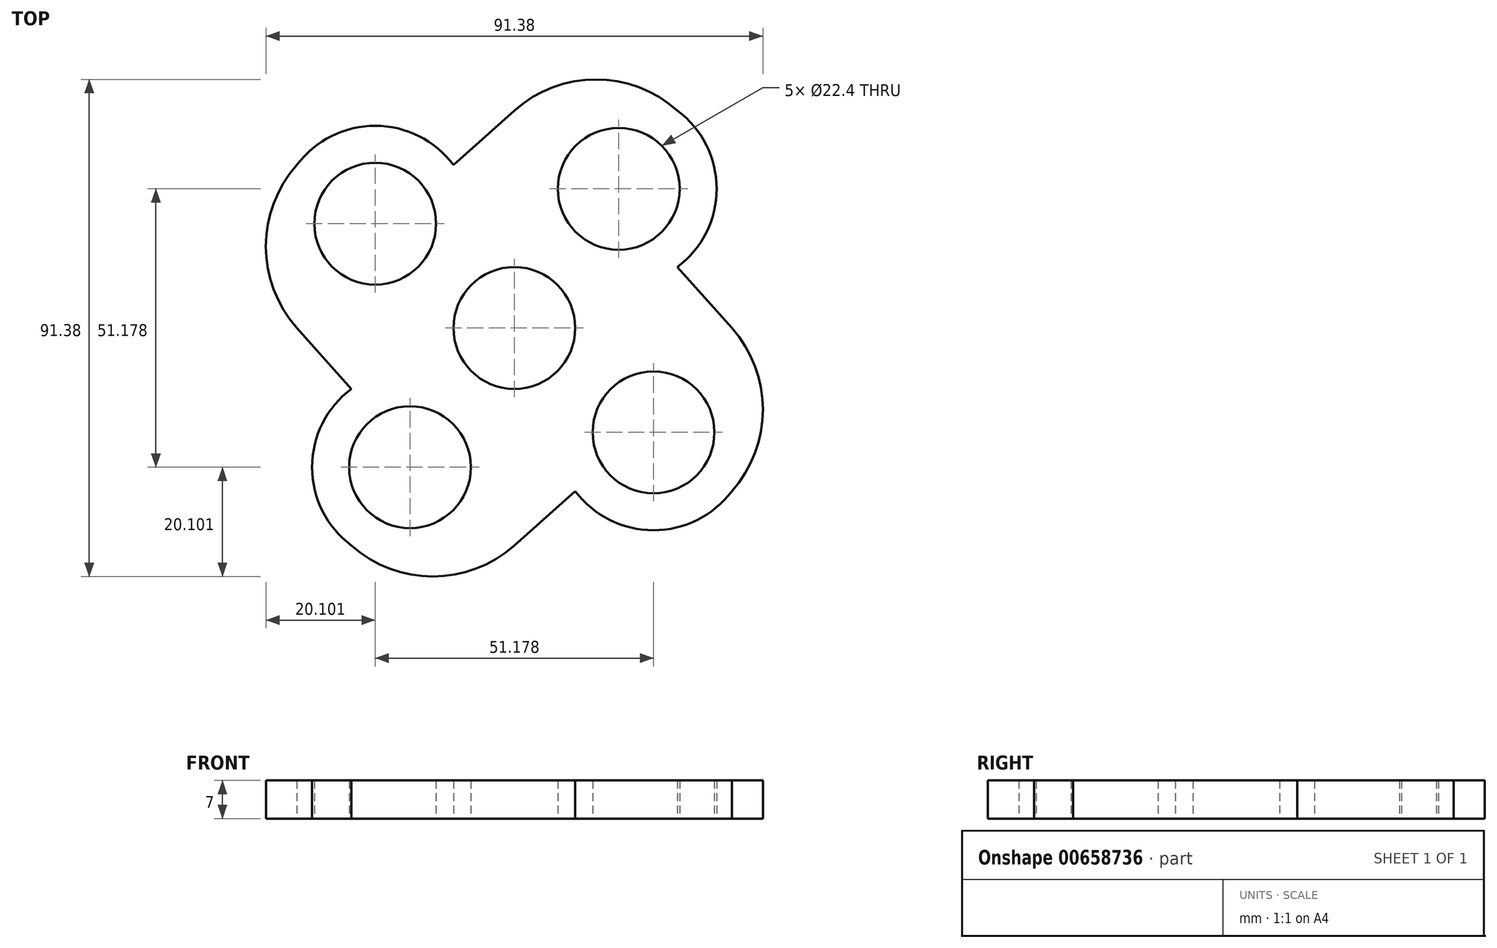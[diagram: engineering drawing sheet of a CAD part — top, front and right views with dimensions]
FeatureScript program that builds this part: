
annotation { "Feature Type Name" : "Feature", "Feature Type Description" : "" }
export const myFeature = defineFeature(function(context is Context, id is Id, definition is map)
    precondition{}
    {
        {
            var Q0;
            Q0=qCreatedBy(makeId("Top.planeOp"),FACE);
            var sketch = newSketch(context, id + "F0", { "sketchPlane" : qUnion([Q0])});
            skCircle(sketch, "E0", {"center": v(0, 0) * mm, "radius": 11.2 * mm});
            skLineSegment(sketch, "E1", {"start": v(0, 11.2) * mm, "end": v(30, 11.2) * mm});
            skLineSegment(sketch, "E2", {"start": v(0, -11.2) * mm, "end": v(-30, -11.2) * mm});
            skLineSegment(sketch, "E3", {"start": v(-11.2, 0) * mm, "end": v(-11.2, 30) * mm});
            skLineSegment(sketch, "E4", {"start": v(11.2, 0) * mm, "end": v(11.2, -30) * mm});
            skLineSegment(sketch, "E5", {"start": v(-11.2, 30) * mm, "end": v(0, 39.98) * mm});
            skLineSegment(sketch, "E6", {"start": v(30, 11.2) * mm, "end": v(39.98, 0) * mm});
            skLineSegment(sketch, "E7", {"start": v(11.2, -30) * mm, "end": v(0, -39.98) * mm});
            skLineSegment(sketch, "E8", {"start": v(-30, -11.2) * mm, "end": v(-39.98, 0) * mm});
            skLineSegment(sketch, "E9", {"start": v(-39.98, 0) * mm, "end": v(-39.98, 30) * mm});
            skLineSegment(sketch, "E10", {"start": v(0, 39.98) * mm, "end": v(30, 39.98) * mm});
            skLineSegment(sketch, "E11", {"start": v(39.98, 0) * mm, "end": v(39.98, -30) * mm});
            skLineSegment(sketch, "E12", {"start": v(0, -39.98) * mm, "end": v(-30, -39.98) * mm});
            skArc(sketch, "E13", {"start": v(-11.2, 30) * mm, "mid": v(-25.59, 37.19) * mm, "end": v(-39.98, 30) * mm});
            skArc(sketch, "E14", {"start": v(30, 11.2) * mm, "mid": v(37.19, 25.59) * mm, "end": v(30, 39.98) * mm});
            skArc(sketch, "E15", {"start": v(11.2, -30) * mm, "mid": v(25.59, -37.19) * mm, "end": v(39.98, -30) * mm});
            skArc(sketch, "E16", {"start": v(-30, -11.2) * mm, "mid": v(-37.19, -25.59) * mm, "end": v(-30, -39.98) * mm});
            skCircle(sketch, "E17", {"center": v(-25.59, 19.19) * mm, "radius": 11.2 * mm});
            skCircle(sketch, "E18", {"center": v(19.19, 25.59) * mm, "radius": 11.2 * mm});
            skCircle(sketch, "E19", {"center": v(25.59, -19.19) * mm, "radius": 11.2 * mm});
            skCircle(sketch, "E20", {"center": v(-19.19, -25.59) * mm, "radius": 11.2 * mm});
            skArc(sketch, "E21", {"start": v(30, 39.98) * mm, "mid": v(15, 45.7) * mm, "end": v(0, 39.98) * mm});
            skArc(sketch, "E22", {"start": v(39.98, -30) * mm, "mid": v(45.7, -15) * mm, "end": v(39.98, 0) * mm});
            skArc(sketch, "E23", {"start": v(-30, -39.98) * mm, "mid": v(-15, -45.7) * mm, "end": v(0, -39.98) * mm});
            skArc(sketch, "E24", {"start": v(-39.98, 30) * mm, "mid": v(-45.7, 15) * mm, "end": v(-39.98, 0) * mm});
            skSolve(sketch);
        }
        {
            var Q0;
            Q0 = qSketchRegion(id + "F0", true);
            extrude(context, id + "F1", {"entities" : qUnion([Q0]), "depth" : 7 * mm, "offsetDistance" : 25 * mm});
        }
    });
